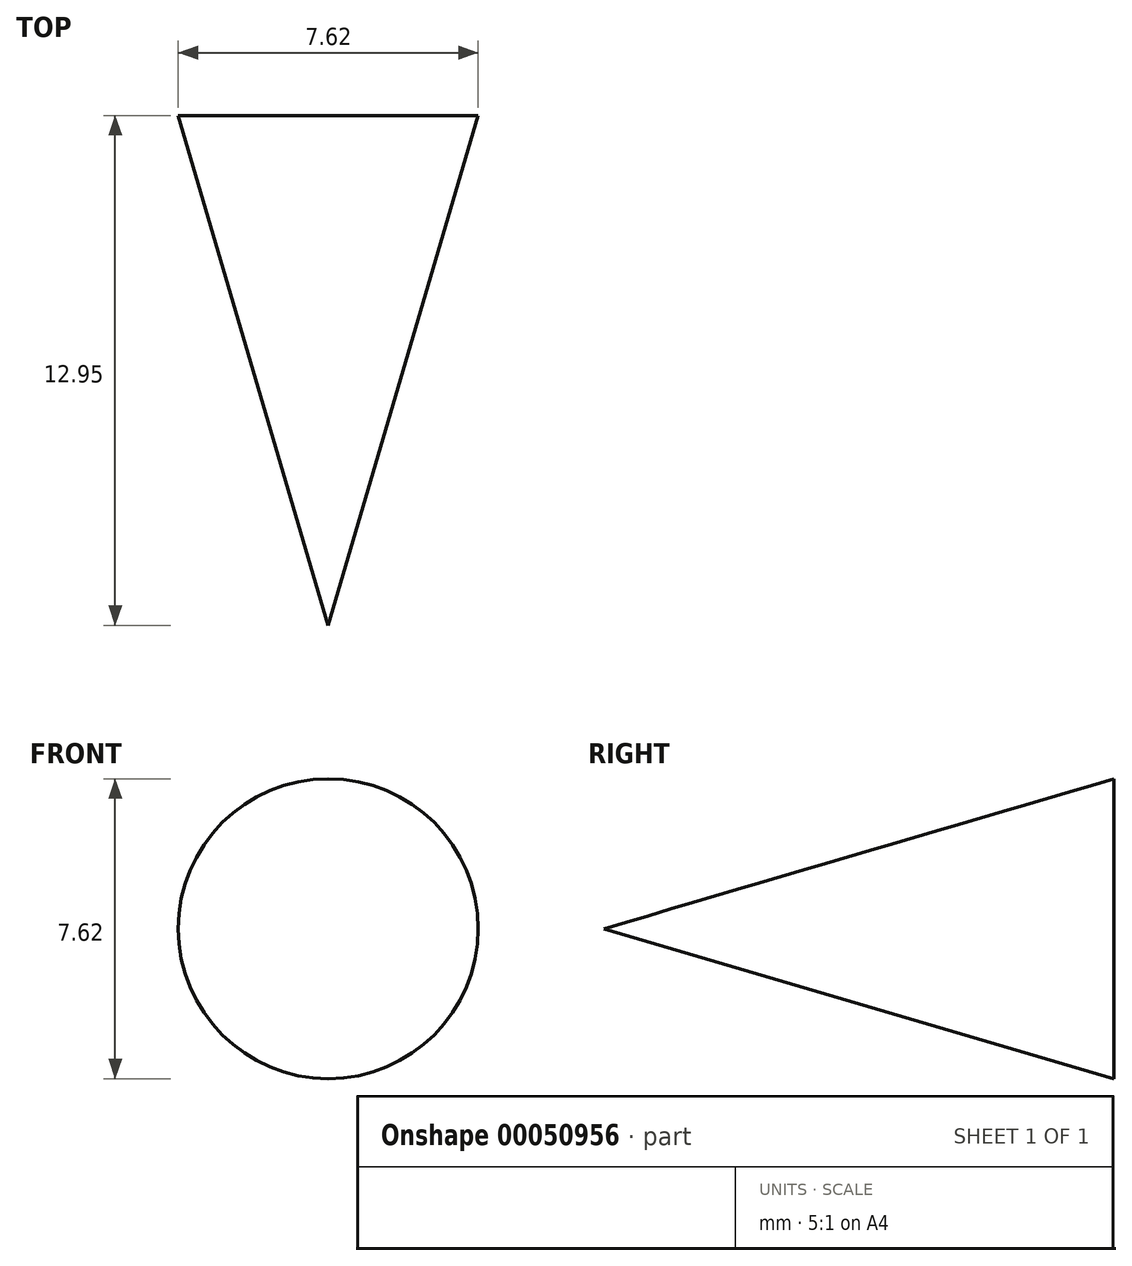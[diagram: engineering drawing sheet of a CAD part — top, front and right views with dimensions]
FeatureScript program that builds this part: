
annotation { "Feature Type Name" : "Feature", "Feature Type Description" : "" }
export const myFeature = defineFeature(function(context is Context, id is Id, definition is map)
    precondition{}
    {
        {
            var Q0;
            Q0=qCreatedBy(makeId("Right.planeOp"),FACE);
            var sketch = newSketch(context, id + "F0", { "sketchPlane" : qUnion([Q0])});
            skLineSegment(sketch, "E0", {"start": v(0, 0) * mm, "end": v(0, 3.8) * mm});
            skLineSegment(sketch, "E1", {"start": v(0, 3.8) * mm, "end": v(-12.95, 0) * mm});
            skLineSegment(sketch, "E2", {"start": v(-12.95, 0) * mm, "end": v(0, 0) * mm});
            skSolve(sketch);
        }
        {
            var Q0;
            Q0=makeQuery(id+"F0.imprint","IMPRINT",FACE,{"disambiguationData":[TD([[makeQuery(id+"F0.imprint","IMPRINT",EDGE,{"derivedFrom":sQuery(id+"F0.wireOp",EDGE,"E0")}),1.0]])]});
            var Q1;
            Q1=sQuery(id+"F0.wireOp",EDGE,"E2");
            revolve(context, id + "F1", {"entities" : qUnion([Q0]), "axis" : qUnion([Q1]), "revolveType" : RevolveType.FULL});
        }
    });
